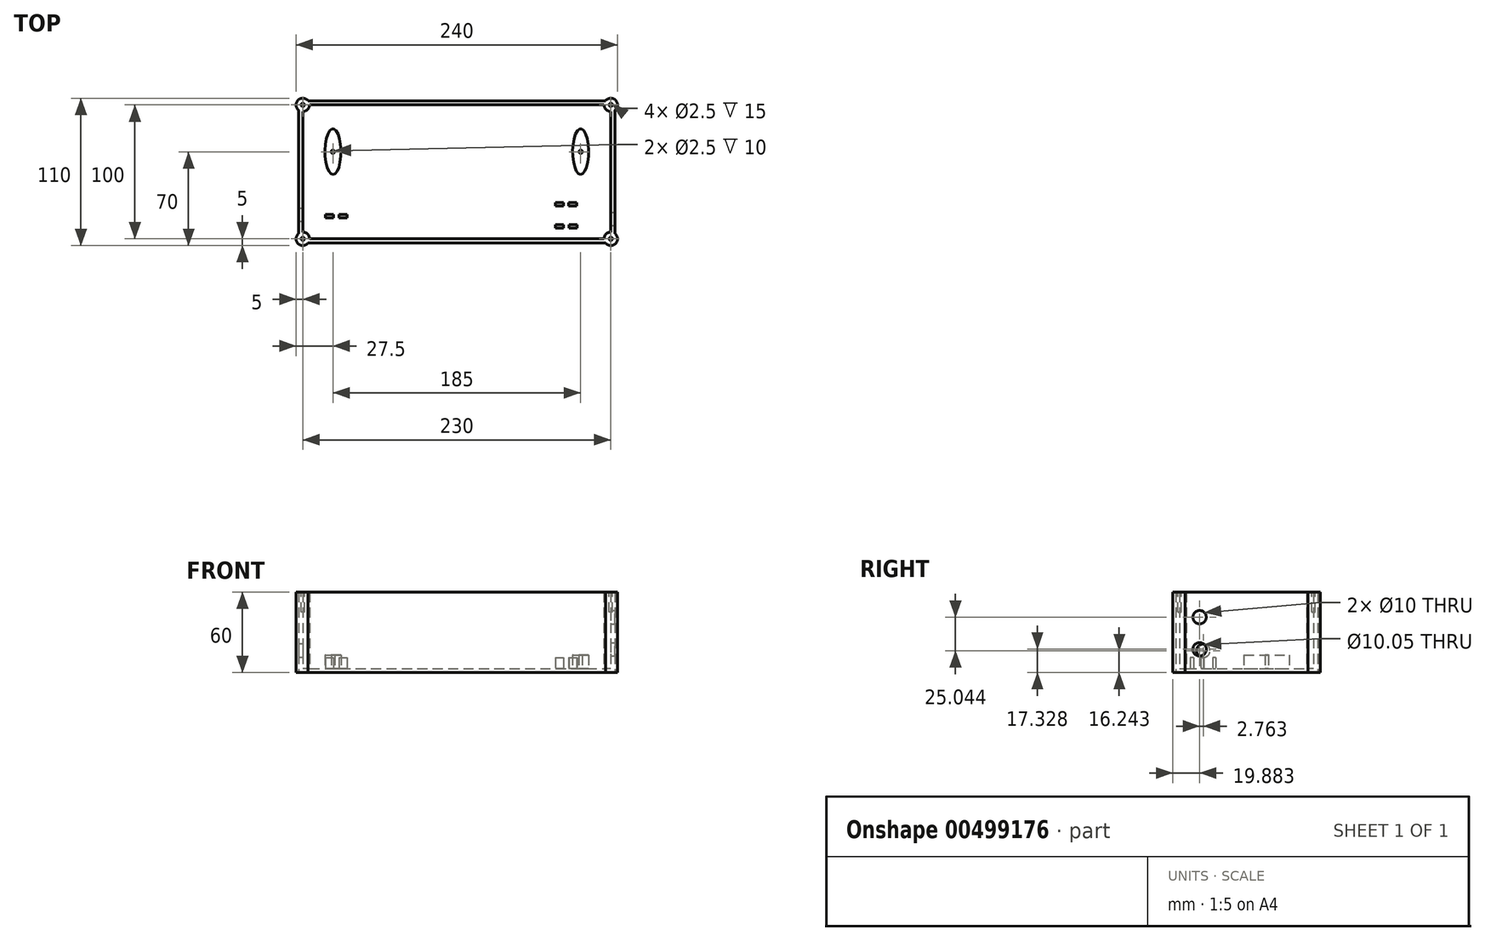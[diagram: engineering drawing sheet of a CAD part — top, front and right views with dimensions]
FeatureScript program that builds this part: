
annotation { "Feature Type Name" : "Feature", "Feature Type Description" : "" }
export const myFeature = defineFeature(function(context is Context, id is Id, definition is map)
    precondition{}
    {
        {
            var Q0;
            Q0=qCreatedBy(makeId("Top.planeOp"),FACE);
            var sketch = newSketch(context, id + "F0", { "sketchPlane" : qUnion([Q0])});
            skLineSegment(sketch, "E0.bottom", {"start": v(0, 0) * mm, "end": v(236, 0) * mm});
            skLineSegment(sketch, "E0.top", {"start": v(0, 106) * mm, "end": v(236, 106) * mm});
            skLineSegment(sketch, "E0.left", {"start": v(0, 0) * mm, "end": v(0, 106) * mm});
            skLineSegment(sketch, "E0.right", {"start": v(236, 0) * mm, "end": v(236, 106) * mm});
            skSolve(sketch);
        }
        {
            var Q0;
            Q0=makeQuery(id+"F0.imprint","IMPRINT",FACE,{"disambiguationData":[TD([[makeQuery(id+"F0.imprint","IMPRINT",EDGE,{"derivedFrom":sQuery(id+"F0.wireOp",EDGE,"E0.bottom")}),1.0]])]});
            extrude(context, id + "F1", {"entities" : qUnion([Q0]), "depth" : 60 * mm});
        }
        {
            var Q0;
            Q0=makeQuery(id+"F1.opExtrude","CAP_FACE",FACE,{"disambiguationData":[OSD([sQuery(id+"F0.wireOp",EDGE,"E0.bottom"),sQuery(id+"F0.wireOp",EDGE,"E0.top"),sQuery(id+"F0.wireOp",EDGE,"E0.left"),sQuery(id+"F0.wireOp",EDGE,"E0.right")])],"isStart":false});
            shell(context, id + "F2", {"entities" : qUnion([Q0]), "thickness" : 3 * mm});
        }
        {
            var Q0;
            Q0=makeQuery(id+"F2.opShell","OFFSET_FACE",FACE,{"disambiguationData":[OSD([sQuery(id+"F0.wireOp",EDGE,"E0.bottom"),sQuery(id+"F0.wireOp",EDGE,"E0.top"),sQuery(id+"F0.wireOp",EDGE,"E0.left"),sQuery(id+"F0.wireOp",EDGE,"E0.right")])]});
            var sketch = newSketch(context, id + "F3", { "sketchPlane" : qUnion([Q0])});
            skLineSegment(sketch, "E1", {"start": v(3, 68) * mm, "end": v(233, 68) * mm, "construction": true});
            skPoint(sketch, "E2", {"position": v(25.5, 68) * mm});
            skPoint(sketch, "E3", {"position": v(210.5, 68) * mm});
            skEllipse(sketch, "E4", {"center": v(25.5, 68) * mm, "majorRadius": 17 * mm, "minorRadius": 6 * mm, "majorAxis": v(0, -1)});
            skEllipse(sketch, "E5", {"center": v(210.5, 68) * mm, "majorRadius": 17 * mm, "minorRadius": 6 * mm, "majorAxis": v(0, -1)});
            skCircle(sketch, "E6", {"center": v(25.5, 68) * mm, "radius": 1.25 * mm});
            skCircle(sketch, "E7", {"center": v(210.5, 68) * mm, "radius": 1.25 * mm});
            skCircle(sketch, "E8", {"center": v(3, 103) * mm, "radius": 5 * mm});
            skCircle(sketch, "E9", {"center": v(233, 3) * mm, "radius": 5 * mm});
            skCircle(sketch, "E10", {"center": v(233, 103) * mm, "radius": 5 * mm});
            skCircle(sketch, "E11", {"center": v(3, 3) * mm, "radius": 5 * mm});
            skSolve(sketch);
        }
        {
            var Q0;
            Q0=makeQuery(id+"F3.imprint","IMPRINT",FACE,{"disambiguationData":[TD([[makeQuery(id+"F3.imprint","IMPRINT",EDGE,{"derivedFrom":sQuery(id+"F3.wireOp",EDGE,"E4")}),1.0]])]});
            var Q1;
            Q1=makeQuery(id+"F3.imprint","IMPRINT",FACE,{"disambiguationData":[TD([[makeQuery(id+"F3.imprint","IMPRINT",EDGE,{"derivedFrom":sQuery(id+"F3.wireOp",EDGE,"E5")}),1.0]])]});
            extrude(context, id + "F4", {"entities" : qUnion([Q0, Q1]), "operationType" : NewBodyOperationType.ADD, "depth" : 10 * mm});
        }
        {
            var Q0;
            Q0=makeQuery(id+"F1.opExtrude","SWEPT_EDGE",EDGE,{"disambiguationData":[OSD([sQuery(id+"F0.wireOp",EDGE,"E0.bottom"),sQuery(id+"F0.wireOp",EDGE,"E0.left")])]});
            var Q1;
            Q1=makeQuery(id+"F1.opExtrude","SWEPT_EDGE",EDGE,{"disambiguationData":[OSD([sQuery(id+"F0.wireOp",EDGE,"E0.top"),sQuery(id+"F0.wireOp",EDGE,"E0.left")])]});
            var Q2;
            Q2=makeQuery(id+"F1.opExtrude","SWEPT_EDGE",EDGE,{"disambiguationData":[OSD([sQuery(id+"F0.wireOp",EDGE,"E0.bottom"),sQuery(id+"F0.wireOp",EDGE,"E0.right")])]});
            var Q3;
            Q3=makeQuery(id+"F1.opExtrude","SWEPT_EDGE",EDGE,{"disambiguationData":[OSD([sQuery(id+"F0.wireOp",EDGE,"E0.top"),sQuery(id+"F0.wireOp",EDGE,"E0.right")])]});
            fillet(context, id + "F5", {"entities" : qUnion([Q0, Q1, Q2, Q3]), "radius" : 5 * mm, "tangentPropagation" : true, "allowEdgeOverflow" : false});
        }
        {
            var Q0;
            {var subQ0=sQuery(id+"F0.wireOp",EDGE,"E0.right");var subQ1=sQuery(id+"F0.wireOp",EDGE,"E0.left");var subQ2=sQuery(id+"F0.wireOp",EDGE,"E0.top");var subQ3=sQuery(id+"F0.wireOp",EDGE,"E0.bottom");Q0=makeQuery(id+"F4.boolean.opBoolean","SPLIT",FACE,{"disambiguationData":[TD([makeQuery(id+"F2.opShell","OFFSET_FACE",FACE,{"disambiguationData":[OSD([subQ3])]})])],"derivedFrom":makeQuery(id+"F2.opShell","OFFSET_FACE",FACE,{"disambiguationData":[OSD([subQ3,subQ2,subQ1,subQ0])]})});}
            var sketch = newSketch(context, id + "F6", { "sketchPlane" : qUnion([Q0])});
            skLineSegment(sketch, "E12", {"start": v(3, 38) * mm, "end": v(233, 38) * mm, "construction": true});
            skSolve(sketch);
        }
        {
            var Q0;
            {var subQ0=sQuery(id+"F3.wireOp",EDGE,"E8");var subQ1=sQuery(id+"F0.wireOp",EDGE,"E0.top");var subQ2=makeQuery(id+"F2.opShell","OFFSET_EDGE",EDGE,{"disambiguationData":[OSD([subQ1]),TDD([makeQuery(id+"F1.opExtrude","CAP_EDGE",EDGE,{"disambiguationData":[OSD([subQ1])],"isStart":true})])]});var subQ3=makeQuery(id+"F3.imprint","INTERSECT",VERTEX,{"derivedFrom":[subQ2,subQ0]});Q0=makeQuery(id+"F3.imprint","IMPRINT",FACE,{"disambiguationData":[TD([[makeQuery(id+"F3.imprint","IMPRINT",EDGE,{"disambiguationData":[TD([[subQ3,1.0]])],"derivedFrom":subQ0}),1.0]])]});}
            var Q1;
            {var subQ0=sQuery(id+"F3.wireOp",EDGE,"E11");var subQ1=sQuery(id+"F0.wireOp",EDGE,"E0.bottom");var subQ2=makeQuery(id+"F2.opShell","OFFSET_EDGE",EDGE,{"disambiguationData":[OSD([subQ1]),TDD([makeQuery(id+"F1.opExtrude","CAP_EDGE",EDGE,{"disambiguationData":[OSD([subQ1])],"isStart":true})])]});var subQ3=makeQuery(id+"F3.imprint","INTERSECT",VERTEX,{"derivedFrom":[subQ2,subQ0]});Q1=makeQuery(id+"F3.imprint","IMPRINT",FACE,{"disambiguationData":[TD([[makeQuery(id+"F3.imprint","IMPRINT",EDGE,{"disambiguationData":[TD([[subQ3,-1.0]])],"derivedFrom":subQ0}),1.0]])]});}
            var Q2;
            {var subQ0=sQuery(id+"F3.wireOp",EDGE,"E10");var subQ1=sQuery(id+"F0.wireOp",EDGE,"E0.top");var subQ2=makeQuery(id+"F2.opShell","OFFSET_EDGE",EDGE,{"disambiguationData":[OSD([subQ1]),TDD([makeQuery(id+"F1.opExtrude","CAP_EDGE",EDGE,{"disambiguationData":[OSD([subQ1])],"isStart":true})])]});var subQ3=makeQuery(id+"F3.imprint","INTERSECT",VERTEX,{"derivedFrom":[subQ2,subQ0]});Q2=makeQuery(id+"F3.imprint","IMPRINT",FACE,{"disambiguationData":[TD([[makeQuery(id+"F3.imprint","IMPRINT",EDGE,{"disambiguationData":[TD([[subQ3,-1.0]])],"derivedFrom":subQ0}),1.0]])]});}
            var Q3;
            {var subQ0=sQuery(id+"F3.wireOp",EDGE,"E9");var subQ1=sQuery(id+"F0.wireOp",EDGE,"E0.bottom");var subQ2=makeQuery(id+"F2.opShell","OFFSET_EDGE",EDGE,{"disambiguationData":[OSD([subQ1]),TDD([makeQuery(id+"F1.opExtrude","CAP_EDGE",EDGE,{"disambiguationData":[OSD([subQ1])],"isStart":true})])]});var subQ3=makeQuery(id+"F3.imprint","INTERSECT",VERTEX,{"derivedFrom":[subQ2,subQ0]});Q3=makeQuery(id+"F3.imprint","IMPRINT",FACE,{"disambiguationData":[TD([[makeQuery(id+"F3.imprint","IMPRINT",EDGE,{"disambiguationData":[TD([[subQ3,1.0]])],"derivedFrom":subQ0}),1.0]])]});}
            var Q4;
            {var subQ0=sQuery(id+"F3.wireOp",EDGE,"E9");var subQ1=sQuery(id+"F0.wireOp",EDGE,"E0.bottom");var subQ2=makeQuery(id+"F2.opShell","OFFSET_EDGE",EDGE,{"disambiguationData":[OSD([subQ1]),TDD([makeQuery(id+"F1.opExtrude","CAP_EDGE",EDGE,{"disambiguationData":[OSD([subQ1])],"isStart":true})])]});var subQ3=makeQuery(id+"F3.imprint","INTERSECT",VERTEX,{"derivedFrom":[subQ2,subQ0]});Q4=makeQuery(id+"F3.imprint","IMPRINT",FACE,{"disambiguationData":[TD([[makeQuery(id+"F3.imprint","IMPRINT",EDGE,{"disambiguationData":[TD([[subQ3,-1.0]])],"derivedFrom":subQ0}),1.0]])]});}
            var Q5;
            {var subQ0=sQuery(id+"F3.wireOp",EDGE,"E11");var subQ1=sQuery(id+"F0.wireOp",EDGE,"E0.bottom");var subQ2=makeQuery(id+"F2.opShell","OFFSET_EDGE",EDGE,{"disambiguationData":[OSD([subQ1]),TDD([makeQuery(id+"F1.opExtrude","CAP_EDGE",EDGE,{"disambiguationData":[OSD([subQ1])],"isStart":true})])]});var subQ3=makeQuery(id+"F3.imprint","INTERSECT",VERTEX,{"derivedFrom":[subQ2,subQ0]});Q5=makeQuery(id+"F3.imprint","IMPRINT",FACE,{"disambiguationData":[TD([[makeQuery(id+"F3.imprint","IMPRINT",EDGE,{"disambiguationData":[TD([[subQ3,1.0]])],"derivedFrom":subQ0}),1.0]])]});}
            var Q6;
            {var subQ0=sQuery(id+"F3.wireOp",EDGE,"E8");var subQ1=sQuery(id+"F0.wireOp",EDGE,"E0.top");var subQ2=makeQuery(id+"F2.opShell","OFFSET_EDGE",EDGE,{"disambiguationData":[OSD([subQ1]),TDD([makeQuery(id+"F1.opExtrude","CAP_EDGE",EDGE,{"disambiguationData":[OSD([subQ1])],"isStart":true})])]});var subQ3=makeQuery(id+"F3.imprint","INTERSECT",VERTEX,{"derivedFrom":[subQ2,subQ0]});Q6=makeQuery(id+"F3.imprint","IMPRINT",FACE,{"disambiguationData":[TD([[makeQuery(id+"F3.imprint","IMPRINT",EDGE,{"disambiguationData":[TD([[subQ3,-1.0]])],"derivedFrom":subQ0}),1.0]])]});}
            var Q7;
            {var subQ0=sQuery(id+"F3.wireOp",EDGE,"E10");var subQ1=sQuery(id+"F0.wireOp",EDGE,"E0.top");var subQ2=makeQuery(id+"F2.opShell","OFFSET_EDGE",EDGE,{"disambiguationData":[OSD([subQ1]),TDD([makeQuery(id+"F1.opExtrude","CAP_EDGE",EDGE,{"disambiguationData":[OSD([subQ1])],"isStart":true})])]});var subQ3=makeQuery(id+"F3.imprint","INTERSECT",VERTEX,{"derivedFrom":[subQ2,subQ0]});Q7=makeQuery(id+"F3.imprint","IMPRINT",FACE,{"disambiguationData":[TD([[makeQuery(id+"F3.imprint","IMPRINT",EDGE,{"disambiguationData":[TD([[subQ3,1.0]])],"derivedFrom":subQ0}),1.0]])]});}
            extrude(context, id + "F7", {"entities" : qUnion([Q0, Q1, Q2, Q3, Q4, Q5, Q6, Q7]), "operationType" : NewBodyOperationType.ADD, "depth" : 57 * mm});
        }
        {
            var Q0;
            {var subQ0=sQuery(id+"F0.wireOp",EDGE,"E0.left");var subQ1=sQuery(id+"F0.wireOp",EDGE,"E0.bottom");var subQ2=sQuery(id+"F0.wireOp",EDGE,"E0.right");var subQ3=sQuery(id+"F0.wireOp",EDGE,"E0.top");Q0=makeQuery(id+"F7.boolean.opBoolean","MERGE",FACE,{"derivedFrom":[makeQuery(id+"F1.opExtrude","CAP_FACE",FACE,{"disambiguationData":[OSD([subQ1,subQ3,subQ0,subQ2])],"isStart":false}),makeQuery(id+"F7.opExtrude","CAP_FACE",FACE,{"disambiguationData":[OSD([subQ3,subQ0,sQuery(id+"F3.wireOp",EDGE,"E8")])],"isStart":false}),makeQuery(id+"F7.opExtrude","CAP_FACE",FACE,{"disambiguationData":[OSD([subQ1,subQ2,sQuery(id+"F3.wireOp",EDGE,"E9")])],"isStart":false}),makeQuery(id+"F7.opExtrude","CAP_FACE",FACE,{"disambiguationData":[OSD([subQ3,subQ2,sQuery(id+"F3.wireOp",EDGE,"E10")])],"isStart":false}),makeQuery(id+"F7.opExtrude","CAP_FACE",FACE,{"disambiguationData":[OSD([subQ1,subQ0,sQuery(id+"F3.wireOp",EDGE,"E11")])],"isStart":false})]});}
            var sketch = newSketch(context, id + "F8", { "sketchPlane" : qUnion([Q0])});
            skCircle(sketch, "E13", {"center": v(233, 103) * mm, "radius": 1.25 * mm});
            skCircle(sketch, "E14", {"center": v(233, 3) * mm, "radius": 1.25 * mm});
            skCircle(sketch, "E15", {"center": v(3, 3) * mm, "radius": 1.25 * mm});
            skCircle(sketch, "E16", {"center": v(3, 103) * mm, "radius": 1.25 * mm});
            skSolve(sketch);
        }
        {
            var Q0;
            Q0=makeQuery(id+"F8.imprint","IMPRINT",FACE,{"disambiguationData":[TD([[makeQuery(id+"F8.imprint","IMPRINT",EDGE,{"derivedFrom":sQuery(id+"F8.wireOp",EDGE,"E14")}),1.0]])]});
            var Q1;
            Q1=makeQuery(id+"F8.imprint","IMPRINT",FACE,{"disambiguationData":[TD([[makeQuery(id+"F8.imprint","IMPRINT",EDGE,{"derivedFrom":sQuery(id+"F8.wireOp",EDGE,"E13")}),1.0]])]});
            var Q2;
            Q2=makeQuery(id+"F8.imprint","IMPRINT",FACE,{"disambiguationData":[TD([[makeQuery(id+"F8.imprint","IMPRINT",EDGE,{"derivedFrom":sQuery(id+"F8.wireOp",EDGE,"E15")}),1.0]])]});
            var Q3;
            Q3=makeQuery(id+"F8.imprint","IMPRINT",FACE,{"disambiguationData":[TD([[makeQuery(id+"F8.imprint","IMPRINT",EDGE,{"derivedFrom":sQuery(id+"F8.wireOp",EDGE,"E16")}),1.0]])]});
            extrude(context, id + "F9", {"entities" : qUnion([Q0, Q1, Q2, Q3]), "operationType" : NewBodyOperationType.REMOVE, "oppositeDirection" : true, "depth" : 15 * mm});
        }
        {
            var Q0;
            Q0=makeQuery(id+"F1.opExtrude","SWEPT_FACE",FACE,{"disambiguationData":[OSD([sQuery(id+"F0.wireOp",EDGE,"E0.right")])]});
            var sketch = newSketch(context, id + "F10", { "sketchPlane" : qUnion([Q0])});
            skCircle(sketch, "E17", {"center": v(17.88, 41.29) * mm, "radius": 5 * mm});
            skCircle(sketch, "E18", {"center": v(17.88, 17.33) * mm, "radius": 5.02 * mm});
            skSolve(sketch);
        }
        {
            var Q0;
            Q0=makeQuery(id+"F10.imprint","IMPRINT",FACE,{"disambiguationData":[TD([[makeQuery(id+"F10.imprint","IMPRINT",EDGE,{"derivedFrom":sQuery(id+"F10.wireOp",EDGE,"E18")}),1.0]])]});
            var Q1;
            Q1=makeQuery(id+"F10.imprint","IMPRINT",FACE,{"disambiguationData":[TD([[makeQuery(id+"F10.imprint","IMPRINT",EDGE,{"derivedFrom":sQuery(id+"F10.wireOp",EDGE,"E17")}),1.0]])]});
            extrude(context, id + "F11", {"entities" : qUnion([Q0, Q1]), "operationType" : NewBodyOperationType.REMOVE, "oppositeDirection" : true, "depth" : 5 * mm});
        }
        {
            var Q0;
            Q0=makeQuery(id+"F1.opExtrude","SWEPT_FACE",FACE,{"disambiguationData":[OSD([sQuery(id+"F0.wireOp",EDGE,"E0.left")])]});
            var sketch = newSketch(context, id + "F12", { "sketchPlane" : qUnion([Q0])});
            skCircle(sketch, "E19", {"center": v(-20.65, 16.24) * mm, "radius": 5 * mm});
            skSolve(sketch);
        }
        {
            var Q0;
            Q0 = qSketchRegion(id + "F12", true);
            extrude(context, id + "F13", {"entities" : qUnion([Q0]), "operationType" : NewBodyOperationType.REMOVE, "oppositeDirection" : true, "depth" : 5 * mm});
        }
        {
            var Q0;
            Q0=makeQuery(id+"F0.imprint","IMPRINT",FACE,{"disambiguationData":[TD([[makeQuery(id+"F0.imprint","IMPRINT",EDGE,{"derivedFrom":sQuery(id+"F0.wireOp",EDGE,"E0.bottom")}),1.0]])]});
            var sketch = newSketch(context, id + "F14", { "sketchPlane" : qUnion([Q0])});
            skLineSegment(sketch, "E20", {"start": v(28.57, 18.78) * mm, "end": v(43.31, 18.78) * mm, "construction": true});
            skLineSegment(sketch, "E21.bottom", {"start": v(19.94, 18.78) * mm, "end": v(25.94, 18.78) * mm});
            skLineSegment(sketch, "E21.top", {"start": v(19.94, 21.18) * mm, "end": v(25.94, 21.18) * mm});
            skLineSegment(sketch, "E21.left", {"start": v(19.94, 18.78) * mm, "end": v(19.94, 21.18) * mm});
            skLineSegment(sketch, "E21.right", {"start": v(25.94, 18.78) * mm, "end": v(25.94, 21.18) * mm});
            skPoint(sketch, "E22.oppositeSnap0", {"position": v(35.94, 18.78) * mm});
            skLineSegment(sketch, "E22.bottom", {"start": v(29.94, 18.78) * mm, "end": v(35.94, 18.78) * mm});
            skLineSegment(sketch, "E22.top", {"start": v(29.94, 21.18) * mm, "end": v(35.94, 21.18) * mm});
            skLineSegment(sketch, "E22.left", {"start": v(29.94, 18.78) * mm, "end": v(29.94, 21.18) * mm});
            skLineSegment(sketch, "E22.right", {"start": v(35.94, 18.78) * mm, "end": v(35.94, 21.18) * mm});
            skSolve(sketch);
        }
        {
            var Q0;
            Q0=makeQuery(id+"F14.imprint","IMPRINT",FACE,{"disambiguationData":[TD([[makeQuery(id+"F14.imprint","IMPRINT",EDGE,{"derivedFrom":sQuery(id+"F14.wireOp",EDGE,"E21.bottom")}),1.0]])]});
            var Q1;
            Q1=makeQuery(id+"F14.imprint","IMPRINT",FACE,{"disambiguationData":[TD([[makeQuery(id+"F14.imprint","IMPRINT",EDGE,{"derivedFrom":sQuery(id+"F14.wireOp",EDGE,"E22.bottom")}),1.0]])]});
            extrude(context, id + "F15", {"entities" : qUnion([Q0, Q1]), "operationType" : NewBodyOperationType.ADD, "depth" : 11 * mm});
        }
        {
            var Q0;
            Q0=makeQuery(id+"F0.imprint","IMPRINT",FACE,{"disambiguationData":[TD([[makeQuery(id+"F0.imprint","IMPRINT",EDGE,{"derivedFrom":sQuery(id+"F0.wireOp",EDGE,"E0.bottom")}),1.0]])]});
            var sketch = newSketch(context, id + "F16", { "sketchPlane" : qUnion([Q0])});
            skLineSegment(sketch, "E23", {"start": v(152.9, 30) * mm, "end": v(217.75, 30) * mm, "construction": true});
            skLineSegment(sketch, "E24.bottom", {"start": v(191.64, 30) * mm, "end": v(197.64, 30) * mm});
            skLineSegment(sketch, "E24.top", {"start": v(191.64, 27.6) * mm, "end": v(197.64, 27.6) * mm});
            skLineSegment(sketch, "E24.left", {"start": v(191.64, 30) * mm, "end": v(191.64, 27.6) * mm});
            skLineSegment(sketch, "E24.right", {"start": v(197.64, 30) * mm, "end": v(197.64, 27.6) * mm});
            skLineSegment(sketch, "E25.bottom", {"start": v(201.64, 30) * mm, "end": v(207.64, 30) * mm});
            skLineSegment(sketch, "E25.top", {"start": v(201.64, 27.6) * mm, "end": v(207.64, 27.6) * mm});
            skLineSegment(sketch, "E25.left", {"start": v(201.64, 30) * mm, "end": v(201.64, 27.6) * mm});
            skLineSegment(sketch, "E25.right", {"start": v(207.64, 30) * mm, "end": v(207.64, 27.6) * mm});
            skLineSegment(sketch, "E26", {"start": v(191.64, 33.08) * mm, "end": v(191.64, 6.87) * mm, "construction": true});
            skLineSegment(sketch, "E27", {"start": v(170.44, 13.4) * mm, "end": v(219.06, 13.4) * mm, "construction": true});
            skLineSegment(sketch, "E28.bottom", {"start": v(191.64, 13.4) * mm, "end": v(197.64, 13.4) * mm});
            skLineSegment(sketch, "E28.top", {"start": v(191.64, 11) * mm, "end": v(197.64, 11) * mm});
            skLineSegment(sketch, "E28.left", {"start": v(191.64, 13.4) * mm, "end": v(191.64, 11) * mm});
            skLineSegment(sketch, "E28.right", {"start": v(197.64, 13.4) * mm, "end": v(197.64, 11) * mm});
            skLineSegment(sketch, "E29.bottom", {"start": v(201.86, 13.4) * mm, "end": v(207.86, 13.4) * mm});
            skLineSegment(sketch, "E29.top", {"start": v(201.86, 11) * mm, "end": v(207.86, 11) * mm});
            skLineSegment(sketch, "E29.left", {"start": v(201.86, 13.4) * mm, "end": v(201.86, 11) * mm});
            skLineSegment(sketch, "E29.right", {"start": v(207.86, 13.4) * mm, "end": v(207.86, 11) * mm});
            skSolve(sketch);
        }
        {
            var Q0;
            Q0 = qSketchRegion(id + "F16", true);
            extrude(context, id + "F17", {"entities" : qUnion([Q0]), "operationType" : NewBodyOperationType.ADD, "depth" : 11 * mm});
        }
        {
            var Q0;
            Q0=makeQuery(id+"F7.opExtrude","CAP_FACE",FACE,{"disambiguationData":[OSD([sQuery(id+"F3.wireOp",EDGE,"E11")])],"isStart":true});
            var Q1;
            Q1=makeQuery(id+"F7.opExtrude","CAP_FACE",FACE,{"disambiguationData":[OSD([sQuery(id+"F3.wireOp",EDGE,"E8")])],"isStart":true});
            var Q2;
            Q2=makeQuery(id+"F7.opExtrude","CAP_FACE",FACE,{"disambiguationData":[OSD([sQuery(id+"F3.wireOp",EDGE,"E10")])],"isStart":true});
            var Q3;
            Q3=makeQuery(id+"F7.opExtrude","CAP_FACE",FACE,{"disambiguationData":[OSD([sQuery(id+"F3.wireOp",EDGE,"E9")])],"isStart":true});
            extrude(context, id + "F18", {"entities" : qUnion([Q0, Q1, Q2, Q3]), "operationType" : NewBodyOperationType.ADD, "depth" : 3 * mm});
        }
    });
